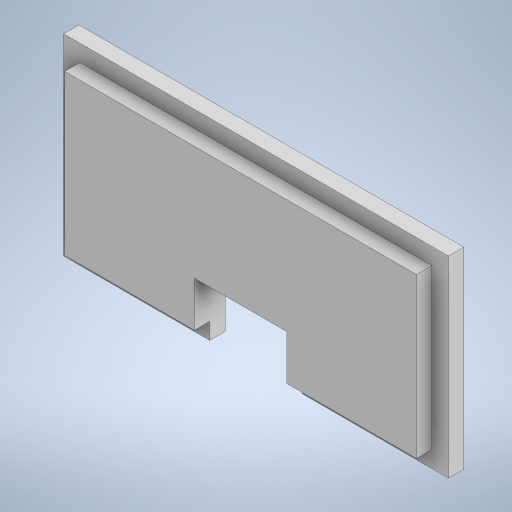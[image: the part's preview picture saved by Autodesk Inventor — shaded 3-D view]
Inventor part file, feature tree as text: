
AUTODESK INVENTOR PART (.ipt)
format: ipt  version: 2024.2 (Build 282272000, 272)  size: 236,032 bytes
history: native  units: mm
features: extrude x3, sketch x3
ambient origin geometry x8: Origin, YZ Plane, XZ Plane, XY Plane, X Axis, Y Axis, Z Axis, Center Point
bodies: Solid1 (feature_tree)
feature tree (6):
  extrude  "Extrusion1"  Depth=25.0mm
  extrude  "Extrusion2"  Depth=45.7mm
  extrude  "Extrusion3"  Depth=2.15mm
  sketch  "Sketch1"  dims[d0=50.0mm d1=25.0mm]
  sketch  "Sketch2"  dims[d2=2.0mm d3=0.0mm d4=45.7mm]
  sketch  "Sketch3"  dims[d5=20.7mm d6=2.15mm d7=2.15mm d8=2.0mm d9=0.0mm d10=12.0mm d11=8.0mm d12=19.0mm d13=0.0mm d14=0.0mm]
